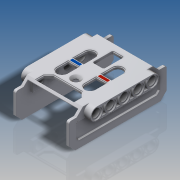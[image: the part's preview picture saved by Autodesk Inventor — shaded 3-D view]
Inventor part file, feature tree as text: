
AUTODESK INVENTOR PART (.ipt)
format: ipt  version: 2016 SP2 (Build 200236200, 236)  size: 927,232 bytes
history: native  units: in
note: dims shown in document units (in); Inventor stores cm internally (conversion verified against a paired STEP export)
features: extrude x14, sketch x6, other x2, mirror x1, revolve x1, fillet x1
ambient origin geometry x8: Origin, YZ Plane, XZ Plane, XY Plane, X Axis, Y Axis, Z Axis, Center Point
bodies: Solid1 (feature_tree)
feature tree (25):
  sketch  "Sketch2"  dims[d0=0.189in d1=1.5748in]
  extrude  "Extrusion1"  Depth=1.5748in
  extrude  "Extrusion2"  Depth=2.2047in
  extrude  "Extrusion3"  Depth=0.1417in
  extrude  "Extrusion4"  Depth=0.063in
  extrude  "Extrusion5"  TaperAngle=0.0deg  [1 undecoded]
  extrude  "Extrusion7"  Depth=0.0157in
  sketch  "Sketch5"  dims[d7=1.6693in d8=0.063in]
  extrude  "Extrusion8"  Depth=0.0157in
  extrude  "Extrusion9"  Depth=0.0157in
  extrude  "Extrusion10"  Depth=0.0157in
  extrude  "Extrusion11"  Depth=0.063in
  mirror  "Mirror1"
  sketch  "Sketch6"  dims[d9=1.2598in d10=0.0in]
  extrude  "Extrusion12"  Depth=0.6299in
  extrude  "Extrusion13"  Depth=0.0315in
  revolve  "Revolution1"  [1 undecoded]
  extrude  "Extrusion14"  TaperAngle=45.0deg  [1 undecoded]
  extrude  "Extrusion15"  Depth=0.0157in TaperAngle=0.0deg
  fillet  "Fillet1"  Radius=0.126in
  sketch  "Sketch3"  dims[d2=0.0472in d3=2.2047in]
  sketch  "Sketch7"  dims[d11=1.1339in d12=0.0in d17=0.3732in d18=0.0472in d19=1.8898in d20=0.0992in d21=0.063in d22=0.6299in d23=0.0315in d24=-0.1826in d25=0.2835in d26=0.315in d27=0.189in d28=0.2441in d39=45.0deg d40=0.1575in d41=0.0in d42=0.126in d43=0.0in d46=0.063in d47=0.0in d48=1.5748in d49=0.0315in d51=0.0945in d52=0.0in d53=0.063in d54=0.0in d55=0.2362in d56=0.063in d57=0.0in d58=0.063in d59=0.0in d60=0.0315in d61=0.0157in d63=0.4661in d64=0.252in d65=0.1402in d66=0.252in d67=0.0945in d68=0.2677in d69=0.315in d70=0.0157in d71=0.8819in d72=0.1181in d74=0.0157in d75=0.315in d76=0.0157in d77=0.0157in d78=0.063in d79=0.2205in d80=0.063in d81=0.0in d82=0.0157in d83=0.0in d84=0.2205in d85=0.1102in d86=0.0157in d87=0.4724in d88=90.0deg d89=0.0in d90=0.0in d91=0.0in d92=0.0in d93=0.0039in d94=0.0157in]
  other  "Blue"
  other  "Red"
  sketch  "Sketch4"  dims[d4=0.1417in d6=0.1417in]
note: 3 required parameter values undecoded (feature->parameter linkage not recoverable at this tier; creation-order binding heuristic only, values carry confidence <= 0.55)